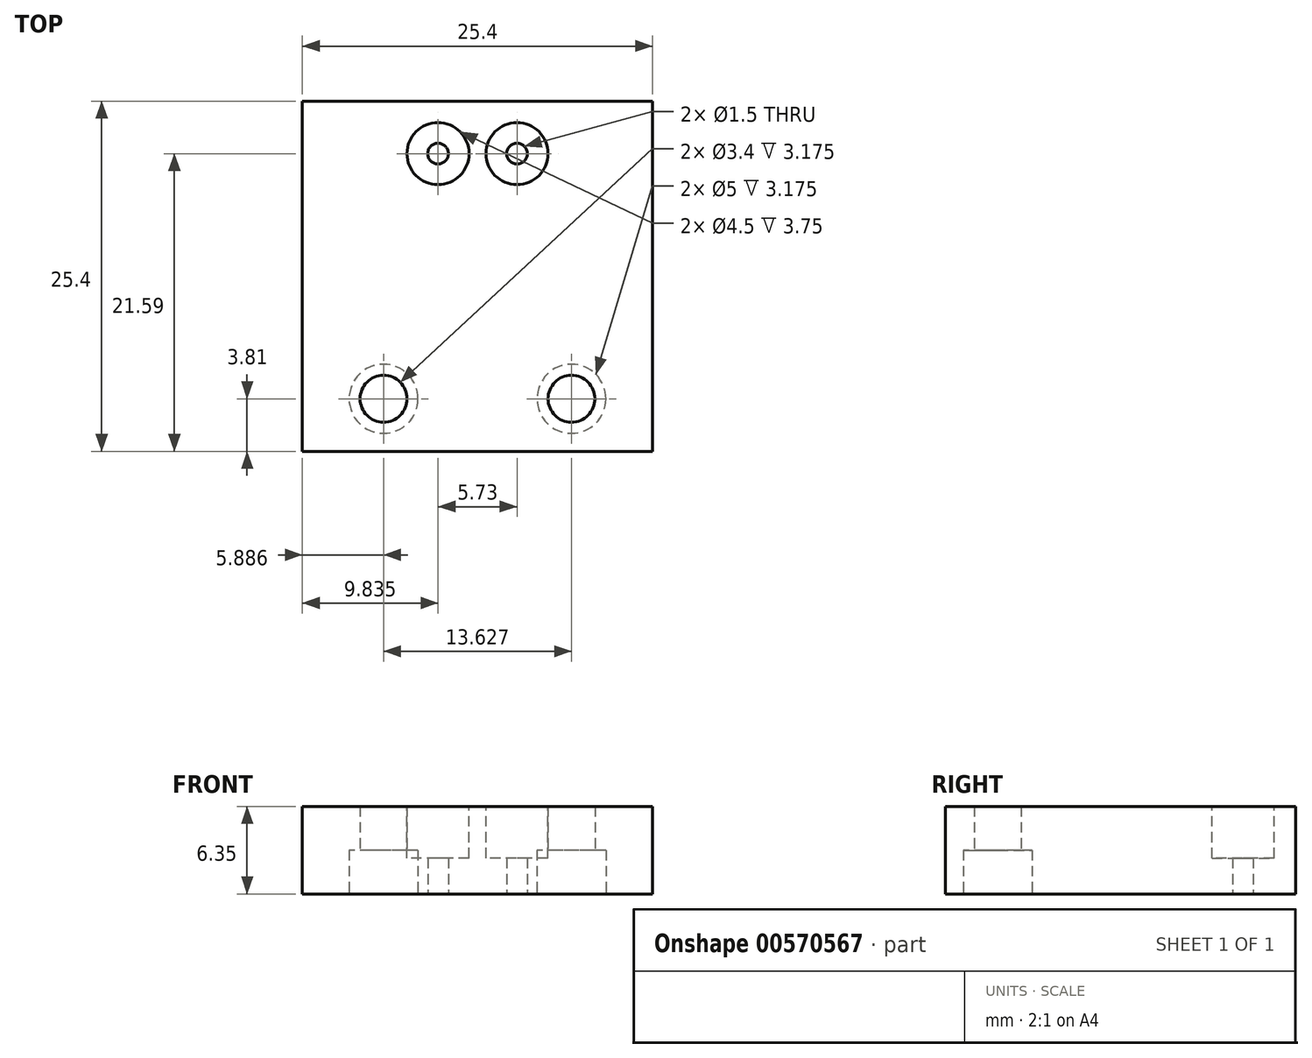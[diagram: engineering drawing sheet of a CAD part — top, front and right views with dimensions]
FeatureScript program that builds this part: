
annotation { "Feature Type Name" : "Feature", "Feature Type Description" : "" }
export const myFeature = defineFeature(function(context is Context, id is Id, definition is map)
    precondition{}
    {
        {
            var Q0;
            Q0=qCreatedBy(makeId("Top.planeOp"),FACE);
            var sketch = newSketch(context, id + "F0", { "sketchPlane" : qUnion([Q0])});
            skLineSegment(sketch, "E0.bottom", {"start": v(12.7, 12.7) * mm, "end": v(-12.7, 12.7) * mm});
            skLineSegment(sketch, "E0.top", {"start": v(12.7, -12.7) * mm, "end": v(-12.7, -12.7) * mm});
            skLineSegment(sketch, "E0.left", {"start": v(12.7, 12.7) * mm, "end": v(12.7, -12.7) * mm});
            skLineSegment(sketch, "E0.right", {"start": v(-12.7, 12.7) * mm, "end": v(-12.7, -12.7) * mm});
            skPoint(sketch, "E0.middle", {"position": v(0, 0) * mm});
            skCircle(sketch, "E1", {"center": v(-2.87, 8.9) * mm, "radius": 0.75 * mm});
            skCircle(sketch, "E2", {"center": v(2.87, 8.9) * mm, "radius": 0.75 * mm});
            skCircle(sketch, "E3", {"center": v(-6.81, -8.89) * mm, "radius": 1.7 * mm});
            skCircle(sketch, "E4", {"center": v(6.81, -8.89) * mm, "radius": 1.7 * mm});
            skSolve(sketch);
        }
        {
            var Q0;
            Q0=makeQuery(id+"F0.imprint","IMPRINT",FACE,{"disambiguationData":[TD([[makeQuery(id+"F0.imprint","IMPRINT",EDGE,{"derivedFrom":sQuery(id+"F0.wireOp",EDGE,"E0.bottom")}),1.0]])]});
            extrude(context, id + "F1", {"entities" : qUnion([Q0]), "depth" : 6.35 * mm, "offsetDistance" : 25.4 * mm});
        }
        {
            var Q0;
            Q0=qCreatedBy(makeId("Top.planeOp"),FACE);
            var sketch = newSketch(context, id + "F2", { "sketchPlane" : qUnion([Q0])});
            skCircle(sketch, "E5", {"center": v(6.81, -8.89) * mm, "radius": 2.5 * mm});
            skCircle(sketch, "E6", {"center": v(-6.81, -8.89) * mm, "radius": 2.5 * mm});
            skSolve(sketch);
        }
        {
            var Q0;
            Q0=makeQuery(id+"F2.imprint","IMPRINT",FACE,{"disambiguationData":[TD([[makeQuery(id+"F2.imprint","IMPRINT",EDGE,{"derivedFrom":sQuery(id+"F2.wireOp",EDGE,"E6")}),1.0]])]});
            var Q1;
            Q1=makeQuery(id+"F2.imprint","IMPRINT",FACE,{"disambiguationData":[TD([[makeQuery(id+"F2.imprint","IMPRINT",EDGE,{"derivedFrom":sQuery(id+"F2.wireOp",EDGE,"X32KD3l4-6vZ9-AaNh-bkeD-w0oz5VFjKeYP")}),1.0]])]});
            var Q2;
            Q2=makeQuery(id+"F2.imprint","IMPRINT",FACE,{"disambiguationData":[TD([[makeQuery(id+"F2.imprint","IMPRINT",EDGE,{"derivedFrom":sQuery(id+"F2.wireOp",EDGE,"jp6bzYoW-vgpv-oe5A-7izM-ru4JRLMfLnF5")}),1.0]])]});
            var Q3;
            Q3=makeQuery(id+"F2.imprint","IMPRINT",FACE,{"disambiguationData":[TD([[makeQuery(id+"F2.imprint","IMPRINT",EDGE,{"derivedFrom":sQuery(id+"F2.wireOp",EDGE,"E5")}),1.0]])]});
            extrude(context, id + "F3", {"entities" : qUnion([Q0, Q1, Q2, Q3]), "operationType" : NewBodyOperationType.REMOVE, "oppositeDirection" : true, "depth" : -6.35 * mm / 2, "offsetDistance" : 25 * mm});
        }
        {
            var Q0;
            Q0=makeQuery(id+"F1.opExtrude","CAP_FACE",FACE,{"disambiguationData":[OSD([sQuery(id+"F0.wireOp",EDGE,"E0.bottom"),sQuery(id+"F0.wireOp",EDGE,"E0.top"),sQuery(id+"F0.wireOp",EDGE,"E0.left"),sQuery(id+"F0.wireOp",EDGE,"E0.right"),sQuery(id+"F0.wireOp",EDGE,"E1"),sQuery(id+"F0.wireOp",EDGE,"E2"),sQuery(id+"F0.wireOp",EDGE,"E3"),sQuery(id+"F0.wireOp",EDGE,"E4")])],"isStart":false});
            var sketch = newSketch(context, id + "F4", { "sketchPlane" : qUnion([Q0])});
            skCircle(sketch, "E7", {"center": v(-2.87, 8.9) * mm, "radius": 2.25 * mm});
            skCircle(sketch, "E8", {"center": v(2.87, 8.9) * mm, "radius": 2.25 * mm});
            skSolve(sketch);
        }
        {
            var Q0;
            Q0 = qSketchRegion(id + "F4", true);
            extrude(context, id + "F5", {"entities" : qUnion([Q0]), "operationType" : NewBodyOperationType.REMOVE, "oppositeDirection" : true, "depth" : 3.75 * mm, "offsetDistance" : 25 * mm});
        }
    });
